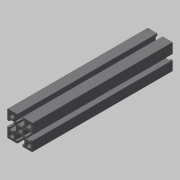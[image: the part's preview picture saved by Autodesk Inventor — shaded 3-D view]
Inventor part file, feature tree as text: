
AUTODESK INVENTOR PART (.ipt)
format: ipt  version: 2021.2 (Build 252289000, 289)  size: 206,336 bytes
history: native  units: in
note: dims shown in document units (in); Inventor stores cm internally (conversion verified against a paired STEP export)
features: other x2, extrude x1, sketch x1, projected_geometry x1
ambient origin geometry x8: Origin, YZ Plane, XZ Plane, XY Plane, X Axis, Y Axis, Z Axis, Center Point
bodies: Body1 (feature_tree)
feature tree (5):
  other  "ソリッド2"
  extrude  "押し出し1"  Depth=6.4961in
  sketch  "スケッチ2"
  projected_geometry  "投影ループ1"
  other  "ソリッド1"
